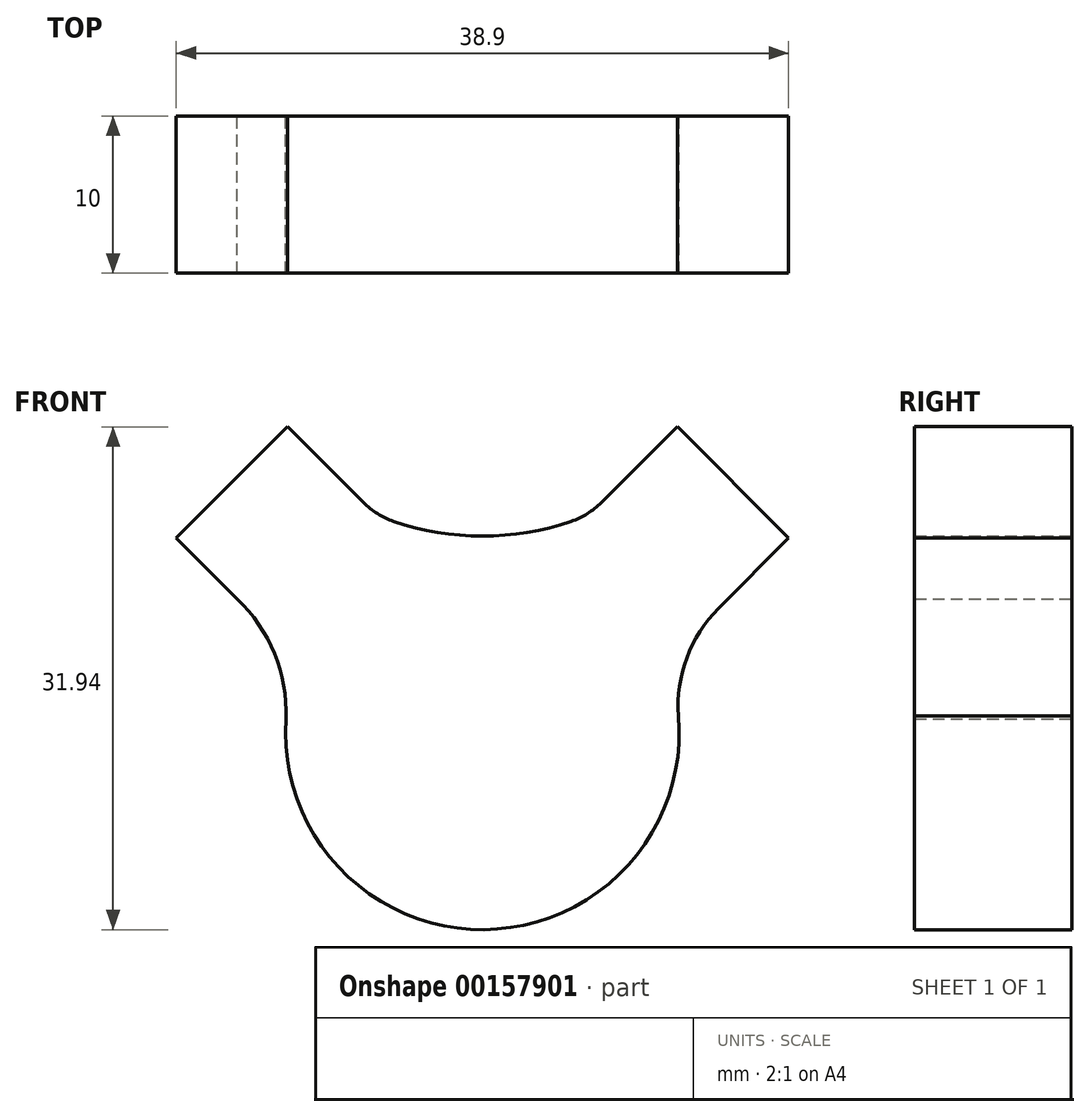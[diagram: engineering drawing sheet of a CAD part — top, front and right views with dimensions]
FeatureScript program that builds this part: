
annotation { "Feature Type Name" : "Feature", "Feature Type Description" : "" }
export const myFeature = defineFeature(function(context is Context, id is Id, definition is map)
    precondition{}
    {
        {
            var Q0;
            Q0=qCreatedBy(makeId("Front.planeOp"),FACE);
            var sketch = newSketch(context, id + "F0", { "sketchPlane" : qUnion([Q0])});
            skArc(sketch, "E0.MirrorC", {"start": v(12.46, -5.3) * mm, "mid": v(0.1, -18.88) * mm, "end": v(-12.46, -5.49) * mm});
            skLineSegment(sketch, "E1.MirrorCS", {"start": v(-7.55, 8.25) * mm, "end": v(-12.36, 13.06) * mm});
            skLineSegment(sketch, "E2.MirrorCS", {"start": v(-15.9, 9.53) * mm, "end": v(-12.36, 13.06) * mm});
            skLineSegment(sketch, "E3.MirrorCS", {"start": v(-15.9, 9.53) * mm, "end": v(-19.44, 6) * mm});
            skLineSegment(sketch, "E4.MirrorCS", {"start": v(-15.57, 2.13) * mm, "end": v(-19.44, 6) * mm});
            skArc(sketch, "E5.MirrorCS", {"start": v(-15.57, 2.13) * mm, "mid": v(-13.2, -1.34) * mm, "end": v(-12.46, -5.49) * mm});
            skLineSegment(sketch, "E6.MirrorCS", {"start": v(15.92, 9.53) * mm, "end": v(12.38, 13.06) * mm});
            skLineSegment(sketch, "E7.MirrorCS", {"start": v(15.92, 9.53) * mm, "end": v(19.46, 6) * mm});
            skPoint(sketch, "E8.visualSharp", {"position": v(-4.56, 5.26) * mm});
            skArc(sketch, "E9", {"start": v(-5.62, 7.05) * mm, "mid": v(0, 6.12) * mm, "end": v(5.64, 7.05) * mm});
            skPoint(sketch, "E10.visualSharp", {"position": v(6.82, 7.5) * mm});
            skArc(sketch, "E10.filletArc", {"start": v(5.64, 7.05) * mm, "mid": v(6.67, 7.54) * mm, "end": v(7.57, 8.25) * mm});
            skPoint(sketch, "E11.visualSharp", {"position": v(-6.8, 7.5) * mm});
            skArc(sketch, "E11.filletArc", {"start": v(-7.55, 8.25) * mm, "mid": v(-6.65, 7.54) * mm, "end": v(-5.62, 7.05) * mm});
            skLineSegment(sketch, "E12", {"start": v(12.38, 13.06) * mm, "end": v(7.57, 8.25) * mm});
            skLineSegment(sketch, "E13", {"start": v(19.46, 6) * mm, "end": v(15, 1.51) * mm});
            skArc(sketch, "E14", {"start": v(15, 1.51) * mm, "mid": v(13, -1.62) * mm, "end": v(12.46, -5.3) * mm});
            skSolve(sketch);
        }
        {
            var Q0;
            Q0 = qSketchRegion(id + "F0", true);
            extrude(context, id + "F1", {"entities" : qUnion([Q0]), "depth" : 10 * mm, "symmetric" : true});
        }
    });
